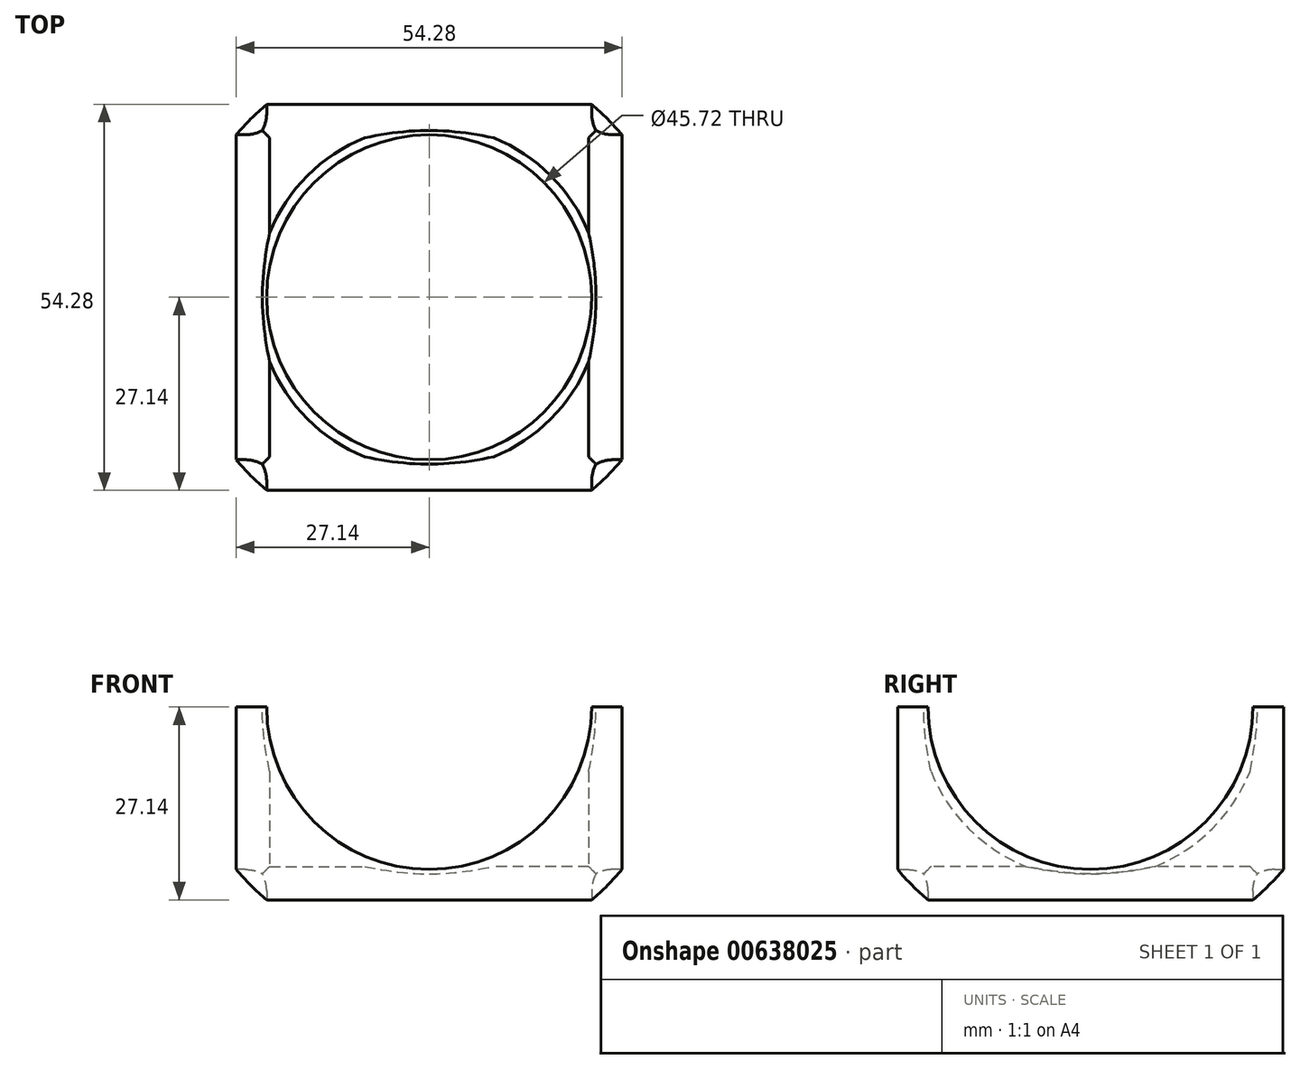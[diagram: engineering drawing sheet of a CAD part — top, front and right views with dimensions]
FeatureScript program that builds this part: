
annotation { "Feature Type Name" : "Feature", "Feature Type Description" : "" }
export const myFeature = defineFeature(function(context is Context, id is Id, definition is map)
    precondition{}
    {
        {
            var Q0;
            Q0=qCreatedBy(makeId("Top.planeOp"),FACE);
            var sketch = newSketch(context, id + "F0", { "sketchPlane" : qUnion([Q0])});
            skCircle(sketch, "E0", {"center": v(0, 0) * mm, "radius": 35.49 * mm});
            skLineSegment(sketch, "E1", {"start": v(0, -35.49) * mm, "end": v(0, 35.49) * mm});
            skSolve(sketch);
        }
        {
            var Q0;
            {var subQ0=sQuery(id+"F0.wireOp",EDGE,"E1");Q0=makeQuery(id+"F0.imprint","IMPRINT",FACE,{"disambiguationData":[TD([[makeQuery(id+"F0.imprint","IMPRINT",EDGE,{"derivedFrom":subQ0}),1.0]])]});}
            var Q1;
            Q1=sQuery(id+"F0.wireOp",EDGE,"E1");
            revolve(context, id + "F1", {"entities" : qUnion([Q0]), "axis" : qUnion([Q1]), "revolveType" : RevolveType.FULL});
        }
        {
            var Q0;
            Q0=qCreatedBy(makeId("Front.planeOp"),FACE);
            var sketch = newSketch(context, id + "F2", { "sketchPlane" : qUnion([Q0])});
            skCircle(sketch, "E2", {"center": v(0, 0) * mm, "radius": 22.86 * mm});
            skSolve(sketch);
        }
        {
            var Q0;
            Q0 = qSketchRegion(id + "F2", true);
            extrude(context, id + "F3", {"entities" : qUnion([Q0]), "operationType" : NewBodyOperationType.REMOVE, "endBound" : BoundingType.SYMMETRIC, "depth" : 76.2 * mm, "offsetDistance" : 25.4 * mm});
        }
        {
            var Q0;
            Q0=qCreatedBy(makeId("Right.planeOp"),FACE);
            var sketch = newSketch(context, id + "F4", { "sketchPlane" : qUnion([Q0])});
            skCircle(sketch, "E3", {"center": v(0, 0) * mm, "radius": 22.86 * mm});
            skSolve(sketch);
        }
        {
            var Q0;
            Q0=makeQuery(id+"F4.imprint","IMPRINT",FACE,{"disambiguationData":[TD([[makeQuery(id+"F4.imprint","IMPRINT",EDGE,{"derivedFrom":sQuery(id+"F4.wireOp",EDGE,"E3")}),1.0]])]});
            extrude(context, id + "F5", {"entities" : qUnion([Q0]), "operationType" : NewBodyOperationType.REMOVE, "endBound" : BoundingType.SYMMETRIC, "depth" : 76.2 * mm, "offsetDistance" : 25.4 * mm});
        }
        {
            var Q0;
            Q0=qCreatedBy(makeId("Top.planeOp"),FACE);
            var sketch = newSketch(context, id + "F6", { "sketchPlane" : qUnion([Q0])});
            skCircle(sketch, "E4", {"center": v(0, 0) * mm, "radius": 22.86 * mm});
            skSolve(sketch);
        }
        {
            var Q0;
            Q0 = qSketchRegion(id + "F6", true);
            extrude(context, id + "F7", {"entities" : qUnion([Q0]), "operationType" : NewBodyOperationType.REMOVE, "endBound" : BoundingType.SYMMETRIC, "depth" : 76.2 * mm, "offsetDistance" : 25.4 * mm});
        }
        {
            var Q0;
            Q0=qCreatedBy(makeId("Top.planeOp"),FACE);
            var sketch = newSketch(context, id + "F8", { "sketchPlane" : qUnion([Q0])});
            skCircle(sketch, "E5", {"center": v(0, 0) * mm, "radius": 33.02 * mm});
            skLineSegment(sketch, "E6", {"start": v(0, 33.02) * mm, "end": v(0, -33.02) * mm});
            skSolve(sketch);
        }
        {
            var Q0;
            {var subQ0=sQuery(id+"F8.wireOp",EDGE,"E6");Q0=makeQuery(id+"F8.imprint","IMPRINT",FACE,{"disambiguationData":[TD([[makeQuery(id+"F8.imprint","IMPRINT",EDGE,{"derivedFrom":subQ0}),-1.0]])]});}
            var Q1;
            Q1=sQuery(id+"F8.wireOp",EDGE,"E6");
            revolve(context, id + "F9", {"operationType" : NewBodyOperationType.REMOVE, "entities" : qUnion([Q0]), "axis" : qUnion([Q1]), "revolveType" : RevolveType.FULL});
        }
        {
            var Q0;
            Q0=makeQuery(id+"F9.boolean.opBoolean","INTERSECT",EDGE,{"derivedFrom":[makeQuery(id+"F5.boolean.opBoolean","COPY",FACE,{"disambiguationData":[OD(1.0)],"derivedFrom":makeQuery(id+"F5.opExtrude","SWEPT_FACE",FACE,{"disambiguationData":[OSD([sQuery(id+"F4.wireOp",EDGE,"E3")])]})}),makeQuery(id+"F9.opRevolve","SWEPT_FACE",FACE,{"disambiguationData":[OSD([sQuery(id+"F8.wireOp",EDGE,"E5")])]})]});
            var Q1;
            Q1=makeQuery(id+"F9.boolean.opBoolean","INTERSECT",EDGE,{"derivedFrom":[makeQuery(id+"F7.boolean.opBoolean","COPY",FACE,{"disambiguationData":[OD(0.0)],"derivedFrom":makeQuery(id+"F7.opExtrude","SWEPT_FACE",FACE,{"disambiguationData":[OSD([sQuery(id+"F6.wireOp",EDGE,"E4")])]})}),makeQuery(id+"F9.opRevolve","SWEPT_FACE",FACE,{"disambiguationData":[OSD([sQuery(id+"F8.wireOp",EDGE,"E5")])]})]});
            var Q2;
            Q2=makeQuery(id+"F9.boolean.opBoolean","INTERSECT",EDGE,{"derivedFrom":[makeQuery(id+"F5.boolean.opBoolean","SPLIT",FACE,{"disambiguationData":[OD(1.0)],"derivedFrom":makeQuery(id+"F3.boolean.opBoolean","COPY",FACE,{"derivedFrom":makeQuery(id+"F3.opExtrude","SWEPT_FACE",FACE,{"disambiguationData":[OSD([sQuery(id+"F2.wireOp",EDGE,"E2")])]})})}),makeQuery(id+"F9.opRevolve","SWEPT_FACE",FACE,{"disambiguationData":[OSD([sQuery(id+"F8.wireOp",EDGE,"E5")])]})]});
            var Q3;
            Q3=makeQuery(id+"F9.boolean.opBoolean","INTERSECT",EDGE,{"derivedFrom":[makeQuery(id+"F5.boolean.opBoolean","SPLIT",FACE,{"disambiguationData":[OD(0.0)],"derivedFrom":makeQuery(id+"F3.boolean.opBoolean","COPY",FACE,{"derivedFrom":makeQuery(id+"F3.opExtrude","SWEPT_FACE",FACE,{"disambiguationData":[OSD([sQuery(id+"F2.wireOp",EDGE,"E2")])]})})}),makeQuery(id+"F9.opRevolve","SWEPT_FACE",FACE,{"disambiguationData":[OSD([sQuery(id+"F8.wireOp",EDGE,"E5")])]})]});
            var Q4;
            Q4=makeQuery(id+"F9.boolean.opBoolean","INTERSECT",EDGE,{"derivedFrom":[makeQuery(id+"F5.boolean.opBoolean","COPY",FACE,{"disambiguationData":[OD(0.0)],"derivedFrom":makeQuery(id+"F5.opExtrude","SWEPT_FACE",FACE,{"disambiguationData":[OSD([sQuery(id+"F4.wireOp",EDGE,"E3")])]})}),makeQuery(id+"F9.opRevolve","SWEPT_FACE",FACE,{"disambiguationData":[OSD([sQuery(id+"F8.wireOp",EDGE,"E5")])]})]});
            var Q5;
            Q5=makeQuery(id+"F9.boolean.opBoolean","INTERSECT",EDGE,{"derivedFrom":[makeQuery(id+"F7.boolean.opBoolean","COPY",FACE,{"disambiguationData":[OD(1.0)],"derivedFrom":makeQuery(id+"F7.opExtrude","SWEPT_FACE",FACE,{"disambiguationData":[OSD([sQuery(id+"F6.wireOp",EDGE,"E4")])]})}),makeQuery(id+"F9.opRevolve","SWEPT_FACE",FACE,{"disambiguationData":[OSD([sQuery(id+"F8.wireOp",EDGE,"E5")])]})]});
            fillet(context, id + "F10", {"entities" : qUnion([Q0, Q1, Q2, Q3, Q4, Q5]), "radius" : 5.08 * mm, "tangentPropagation" : true, "allowEdgeOverflow" : false});
        }
        {
            var Q0;
            Q0=qCreatedBy(makeId("Front.planeOp"),FACE);
            var sketch = newSketch(context, id + "F11", { "sketchPlane" : qUnion([Q0])});
            skLineSegment(sketch, "E7.bottom", {"start": v(-37.9, 28.56) * mm, "end": v(45.42, 28.56) * mm});
            skLineSegment(sketch, "E7.top", {"start": v(-37.9, 0) * mm, "end": v(45.42, 0) * mm});
            skLineSegment(sketch, "E7.left", {"start": v(-37.9, 28.56) * mm, "end": v(-37.9, 0) * mm});
            skLineSegment(sketch, "E7.right", {"start": v(45.42, 28.56) * mm, "end": v(45.42, 0) * mm});
            skSolve(sketch);
        }
        {
            var Q0;
            Q0=makeQuery(id+"F11.imprint","IMPRINT",FACE,{"disambiguationData":[TD([[makeQuery(id+"F11.imprint","IMPRINT",EDGE,{"derivedFrom":sQuery(id+"F11.wireOp",EDGE,"E7.bottom")}),-1.0]])]});
            extrude(context, id + "F12", {"entities" : qUnion([Q0]), "operationType" : NewBodyOperationType.REMOVE, "endBound" : BoundingType.SYMMETRIC, "depth" : 76.2 * mm, "offsetDistance" : 25.4 * mm});
        }
    });
